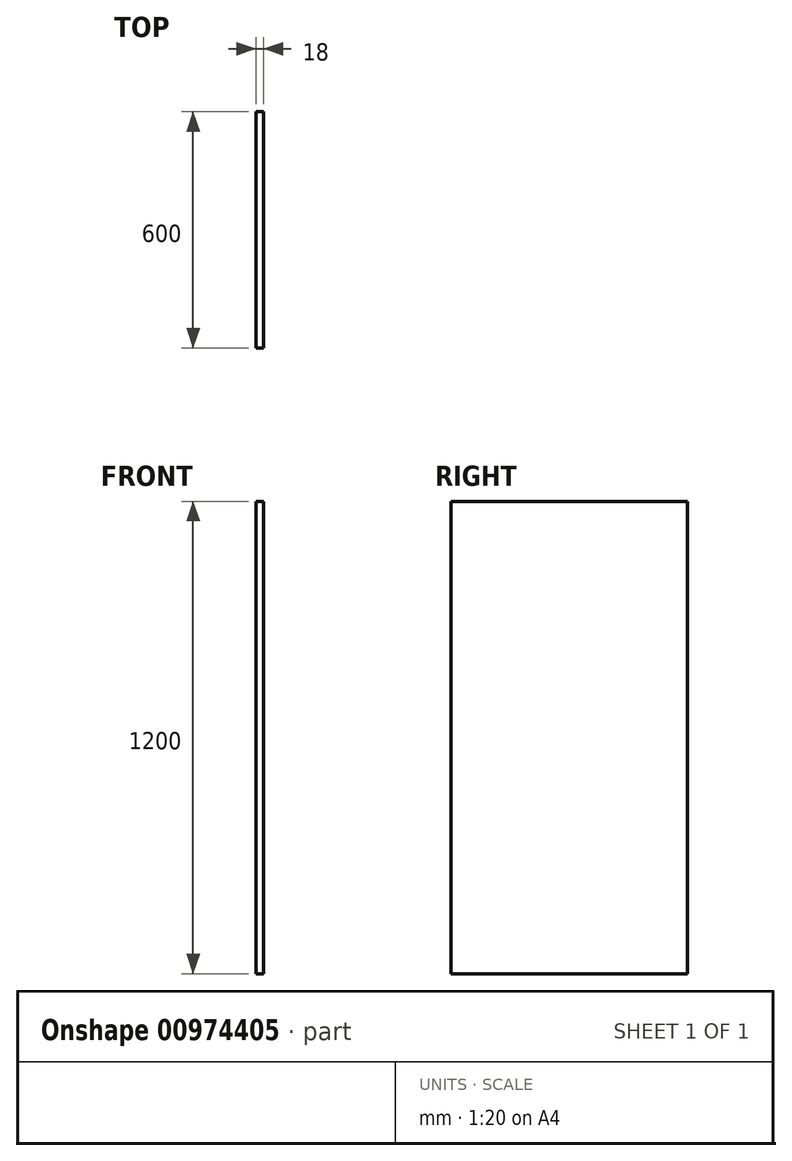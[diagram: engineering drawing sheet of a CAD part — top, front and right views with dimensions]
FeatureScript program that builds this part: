
annotation { "Feature Type Name" : "Feature", "Feature Type Description" : "" }
export const myFeature = defineFeature(function(context is Context, id is Id, definition is map)
    precondition{}
    {
        {
            var Q0;
            Q0=qCreatedBy(makeId("Right.planeOp"),FACE);
            var sketch = newSketch(context, id + "F0", { "sketchPlane" : qUnion([Q0])});
            skLineSegment(sketch, "E0.bottom", {"start": v(300, 600) * mm, "end": v(-300, 600) * mm});
            skLineSegment(sketch, "E0.top", {"start": v(300, -600) * mm, "end": v(-300, -600) * mm});
            skLineSegment(sketch, "E0.left", {"start": v(300, 600) * mm, "end": v(300, -600) * mm});
            skLineSegment(sketch, "E0.right", {"start": v(-300, 600) * mm, "end": v(-300, -600) * mm});
            skPoint(sketch, "E0.middle", {"position": v(0, 0) * mm});
            skLineSegment(sketch, "E1", {"start": v(300, 1400) * mm, "end": v(300, 600) * mm});
            skSolve(sketch);
        }
        {
            var Q0;
            Q0=makeQuery(id+"F0.imprint","IMPRINT",FACE,{"disambiguationData":[TD([[makeQuery(id+"F0.imprint","IMPRINT",EDGE,{"derivedFrom":sQuery(id+"F0.wireOp",EDGE,"E0.bottom")}),1.0]])]});
            extrude(context, id + "F1", {"entities" : qUnion([Q0]), "depth" : 18 * mm, "offsetDistance" : 25 * mm});
        }
        {
            var Q0;
            {var subQ0=sQuery(id+"F0.wireOp",EDGE,"E0.top");Q0=makeQuery(id+"F0.imprint","IMPRINT",FACE,{"disambiguationData":[TD([[makeQuery(id+"F0.imprint","IMPRINT",EDGE,{"derivedFrom":subQ0}),-1.0]])]});}
            extrude(context, id + "F2", {"entities" : qUnion([Q0]), "operationType" : NewBodyOperationType.ADD, "depth" : 18 * mm, "offsetDistance" : 25 * mm});
        }
    });
